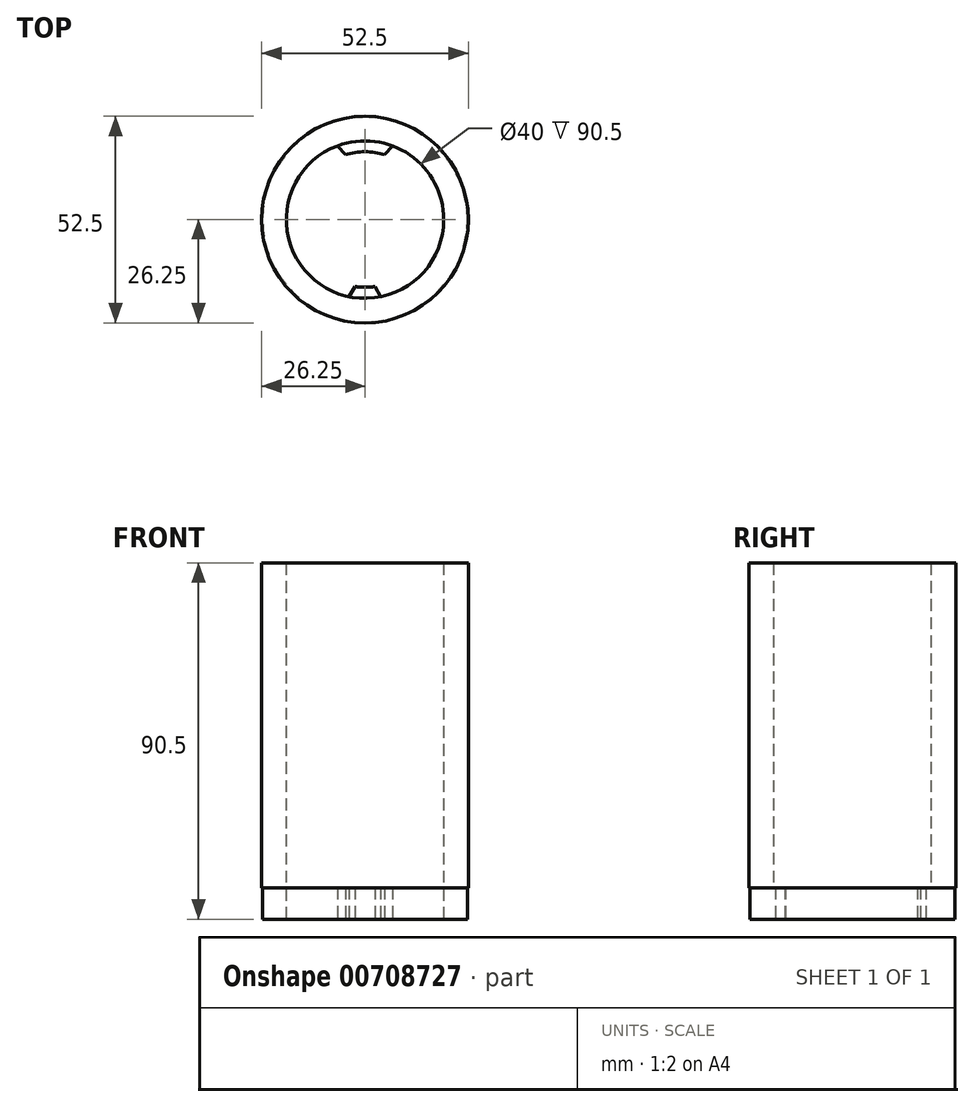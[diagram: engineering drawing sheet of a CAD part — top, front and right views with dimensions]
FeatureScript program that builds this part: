
annotation { "Feature Type Name" : "Feature", "Feature Type Description" : "" }
export const myFeature = defineFeature(function(context is Context, id is Id, definition is map)
    precondition{}
    {
        {
            var Q0;
            Q0=qCreatedBy(makeId("Top.planeOp"),FACE);
            var sketch = newSketch(context, id + "F0", { "sketchPlane" : qUnion([Q0])});
            skArc(sketch, "E0", {"start": v(4, -19.6) * mm, "mid": v(19.94, -1.56) * mm, "end": v(7, 18.73) * mm});
            skCircle(sketch, "E1", {"center": v(0, 0) * mm, "radius": 26 * mm});
            skLineSegment(sketch, "E2", {"start": v(-4, -19.6) * mm, "end": v(-2.5, -17) * mm});
            skLineSegment(sketch, "E3.MirrorCS", {"start": v(4, -19.6) * mm, "end": v(2.5, -17) * mm});
            skArc(sketch, "E4", {"start": v(-2.5, -17) * mm, "mid": v(0, -17.18) * mm, "end": v(2.5, -17) * mm});
            skLineSegment(sketch, "E5", {"start": v(-7, 18.73) * mm, "end": v(-5, 16.5) * mm});
            skLineSegment(sketch, "E6.MirrorCS", {"start": v(7, 18.73) * mm, "end": v(5, 16.5) * mm});
            skArc(sketch, "E7", {"start": v(5, 16.5) * mm, "mid": v(0, 17.25) * mm, "end": v(-5, 16.5) * mm});
            skPoint(sketch, "E7.third.point", {"position": v(2.58, -16.8) * mm});
            skArc(sketch, "E8.trimOffspring", {"start": v(-7, 18.73) * mm, "mid": v(-19.94, -1.56) * mm, "end": v(-4, -19.6) * mm});
            skSolve(sketch);
        }
        {
            var Q0;
            Q0 = qSketchRegion(id + "F0", true);
            extrude(context, id + "F1", {"entities" : qUnion([Q0]), "depth" : 8 * mm, "offsetDistance" : 25 * mm});
        }
        {
            var Q0;
            Q0=makeQuery(id+"F1.opExtrude","CAP_FACE",FACE,{"disambiguationData":[OSD([sQuery(id+"F0.wireOp",EDGE,"E0"),sQuery(id+"F0.wireOp",EDGE,"E1"),sQuery(id+"F0.wireOp",EDGE,"E2"),sQuery(id+"F0.wireOp",EDGE,"E3.MirrorCS"),sQuery(id+"F0.wireOp",EDGE,"E4"),sQuery(id+"F0.wireOp",EDGE,"E5"),sQuery(id+"F0.wireOp",EDGE,"E6.MirrorCS"),sQuery(id+"F0.wireOp",EDGE,"E7"),sQuery(id+"F0.wireOp",EDGE,"E8.trimOffspring")])],"isStart":false});
            var sketch = newSketch(context, id + "F2", { "sketchPlane" : qUnion([Q0])});
            skCircle(sketch, "E9", {"center": v(0, 0) * mm, "radius": 20 * mm});
            skCircle(sketch, "E10", {"center": v(0, 0) * mm, "radius": 26.25 * mm});
            skSolve(sketch);
        }
        {
            var Q0;
            Q0 = qSketchRegion(id + "F2", true);
            extrude(context, id + "F3", {"entities" : qUnion([Q0]), "operationType" : NewBodyOperationType.ADD, "depth" : 82.5 * mm, "offsetDistance" : 25 * mm});
        }
    });
